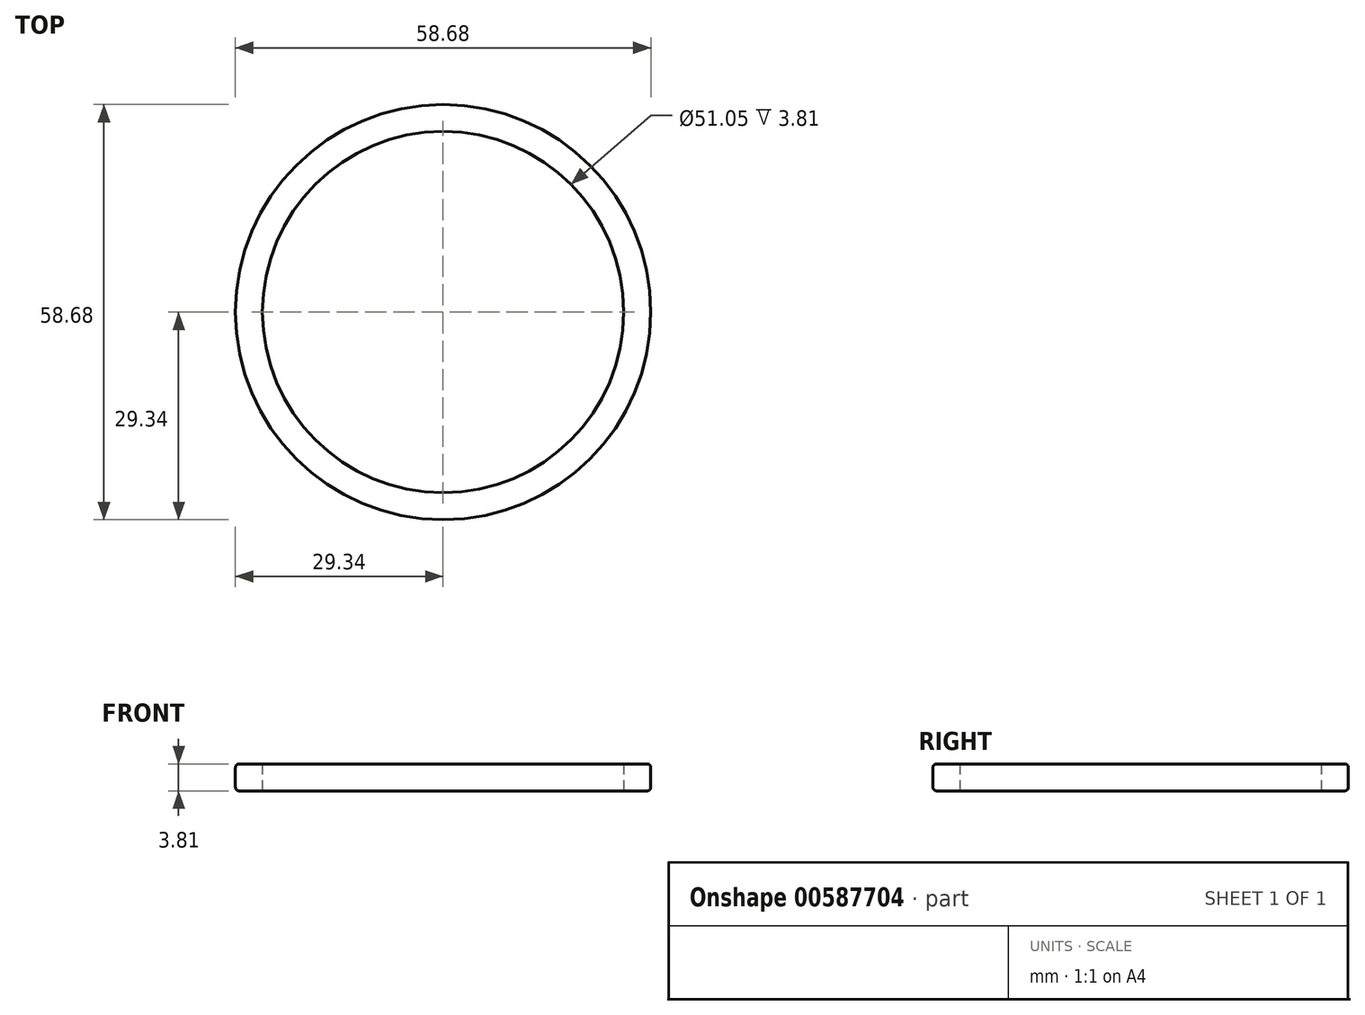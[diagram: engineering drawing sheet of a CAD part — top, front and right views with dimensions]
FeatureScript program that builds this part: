
annotation { "Feature Type Name" : "Feature", "Feature Type Description" : "" }
export const myFeature = defineFeature(function(context is Context, id is Id, definition is map)
    precondition{}
    {
        {
            var Q0;
            Q0=qCreatedBy(makeId("Top.planeOp"),FACE);
            var sketch = newSketch(context, id + "F0", { "sketchPlane" : qUnion([Q0])});
            skCircle(sketch, "E0", {"center": v(0, 0) * mm, "radius": 25.53 * mm});
            skCircle(sketch, "E1.0", {"center": v(0, 0) * mm, "radius": 29.34 * mm});
            skSolve(sketch);
        }
        {
            var Q0;
            Q0=makeQuery(id+"F0.imprint","IMPRINT",FACE,{"disambiguationData":[TD([[makeQuery(id+"F0.imprint","IMPRINT",EDGE,{"derivedFrom":sQuery(id+"F0.wireOp",EDGE,"E0")}),-1.0]])]});
            extrude(context, id + "F1", {"entities" : qUnion([Q0]), "depth" : 3.8 * mm, "offsetDistance" : 25.4 * mm});
        }
        {
            var Q0;
            Q0=makeQuery(id+"F1.opExtrude","CAP_EDGE",EDGE,{"disambiguationData":[OSD([sQuery(id+"F0.wireOp",EDGE,"E1.0")])],"isStart":false});
            fillet(context, id + "F2", {"entities" : qUnion([Q0]), "radius" : 0.5 * mm, "tangentPropagation" : true, "allowEdgeOverflow" : false});
        }
        {
            var Q0;
            Q0=makeQuery(id+"F1.opExtrude","CAP_EDGE",EDGE,{"disambiguationData":[OSD([sQuery(id+"F0.wireOp",EDGE,"E1.0")])],"isStart":true});
            fillet(context, id + "F3", {"entities" : qUnion([Q0]), "radius" : 0.5 * mm, "tangentPropagation" : true, "allowEdgeOverflow" : false});
        }
    });
